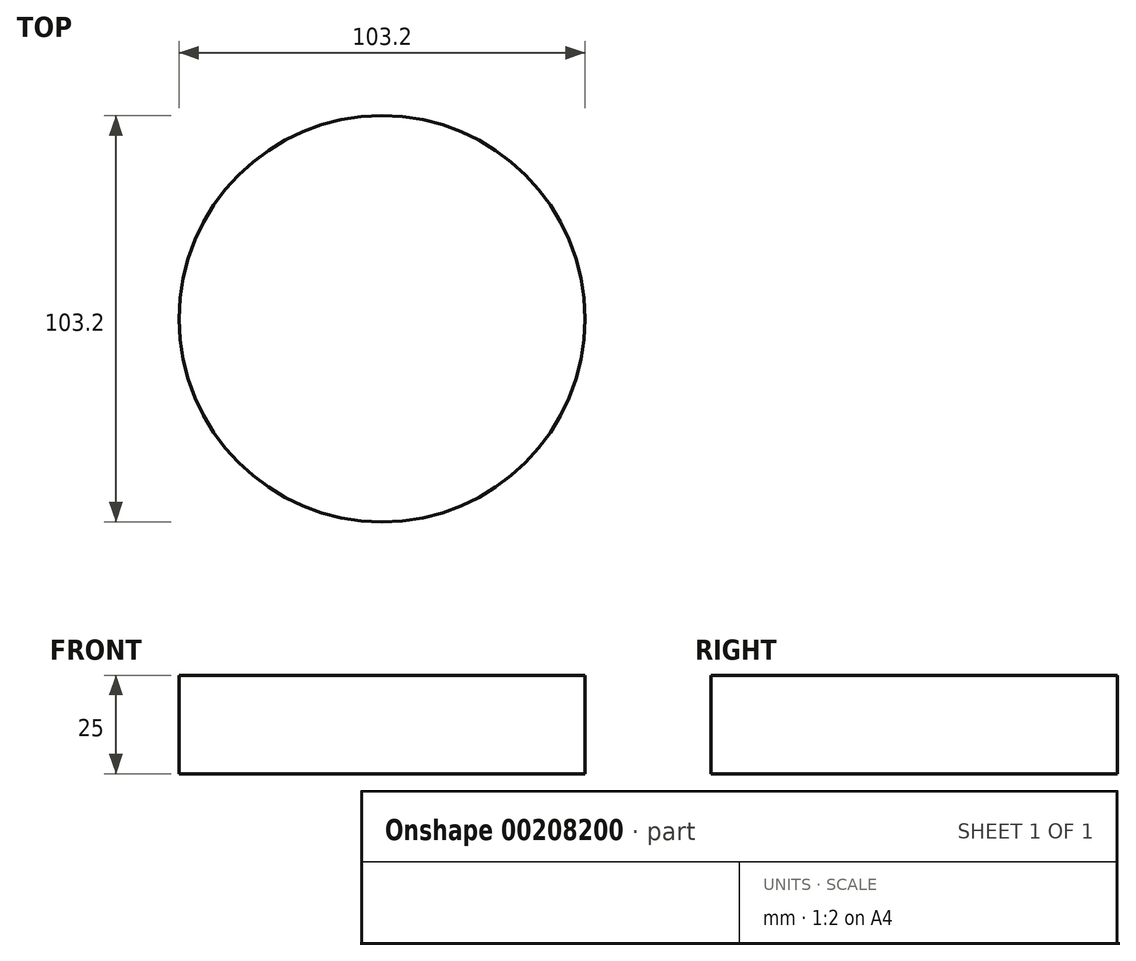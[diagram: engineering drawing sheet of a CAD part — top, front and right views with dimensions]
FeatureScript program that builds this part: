
annotation { "Feature Type Name" : "Feature", "Feature Type Description" : "" }
export const myFeature = defineFeature(function(context is Context, id is Id, definition is map)
    precondition{}
    {
        {
            var Q0;
            Q0=qCreatedBy(makeId("Top.planeOp"),FACE);
            var sketch = newSketch(context, id + "F0", { "sketchPlane" : qUnion([Q0])});
            skCircle(sketch, "E0", {"center": v(0, 0) * mm, "radius": 51.6 * mm});
            skSolve(sketch);
        }
        {
            var Q0;
            Q0=makeQuery(id+"F0.imprint","IMPRINT",FACE,{"disambiguationData":[TD([[makeQuery(id+"F0.imprint","IMPRINT",EDGE,{"derivedFrom":sQuery(id+"F0.wireOp",EDGE,"E0")}),1.0]])]});
            extrude(context, id + "F1", {"entities" : qUnion([Q0]), "depth" : 25 * mm});
        }
    });
